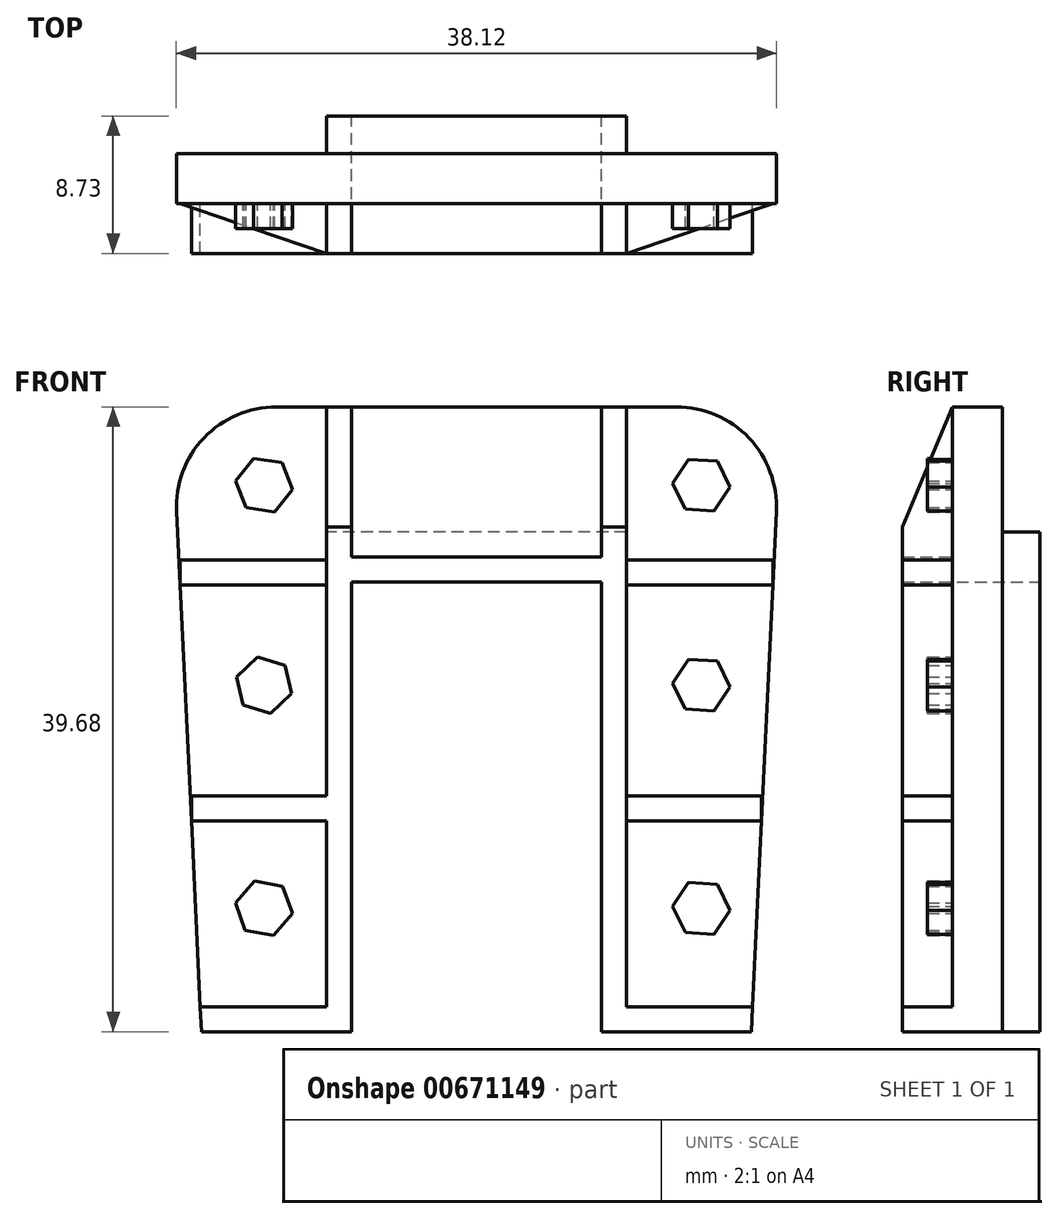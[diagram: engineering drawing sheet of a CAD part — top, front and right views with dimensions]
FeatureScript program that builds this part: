
annotation { "Feature Type Name" : "Feature", "Feature Type Description" : "" }
export const myFeature = defineFeature(function(context is Context, id is Id, definition is map)
    precondition{}
    {
        {
            var Q0;
            Q0=qCreatedBy(makeId("Front.planeOp"),FACE);
            var sketch = newSketch(context, id + "F0", { "sketchPlane" : qUnion([Q0])});
            skLineSegment(sketch, "E0", {"start": v(18.33, 6.17) * mm, "end": v(18.33, 34.74) * mm});
            skLineSegment(sketch, "E1", {"start": v(18.33, 34.74) * mm, "end": v(34.2, 34.74) * mm});
            skLineSegment(sketch, "E2", {"start": v(34.2, 34.74) * mm, "end": v(34.2, 6.17) * mm});
            skLineSegment(sketch, "E3", {"start": v(34.2, 6.17) * mm, "end": v(43.73, 6.17) * mm});
            skLineSegment(sketch, "E4", {"start": v(43.73, 6.17) * mm, "end": v(45.32, 39.2) * mm});
            skLineSegment(sketch, "E5", {"start": v(38.98, 45.85) * mm, "end": v(13.56, 45.85) * mm});
            skLineSegment(sketch, "E6", {"start": v(7.22, 39.2) * mm, "end": v(8.8, 6.17) * mm});
            skLineSegment(sketch, "E7", {"start": v(8.8, 6.17) * mm, "end": v(18.33, 6.17) * mm});
            skPoint(sketch, "E8.visualSharp", {"position": v(6.9, 45.85) * mm});
            skArc(sketch, "E8.filletArc", {"start": v(13.56, 45.85) * mm, "mid": v(8.97, 43.88) * mm, "end": v(7.22, 39.2) * mm});
            skPoint(sketch, "E9.visualSharp", {"position": v(45.64, 45.85) * mm});
            skArc(sketch, "E9.filletArc", {"start": v(45.32, 39.2) * mm, "mid": v(43.57, 43.88) * mm, "end": v(38.98, 45.85) * mm});
            skSolve(sketch);
        }
        {
            var Q0;
            Q0=qSketchRegion(id+"F0",true);
            extrude(context, id + "F1", {"entities" : qUnion([Q0]), "depth" : 3.17 * mm});
        }
        {
            var Q0;
            Q0=makeQuery(id+"F1.opExtrude","CAP_FACE",FACE,{"disambiguationData":[OSD([sQuery(id+"F0.wireOp",EDGE,"E0"),sQuery(id+"F0.wireOp",EDGE,"E1"),sQuery(id+"F0.wireOp",EDGE,"E2"),sQuery(id+"F0.wireOp",EDGE,"E3"),sQuery(id+"F0.wireOp",EDGE,"E4"),sQuery(id+"F0.wireOp",EDGE,"E5"),sQuery(id+"F0.wireOp",EDGE,"E6"),sQuery(id+"F0.wireOp",EDGE,"E7"),sQuery(id+"F0.wireOp",EDGE,"E8.filletArc"),sQuery(id+"F0.wireOp",EDGE,"E9.filletArc")])],"isStart":true});
            var sketch = newSketch(context, id + "F2", { "sketchPlane" : qUnion([Q0])});
            skLineSegment(sketch, "E10", {"start": v(-35.8, 6.17) * mm, "end": v(-35.8, 37.92) * mm});
            skLineSegment(sketch, "E11", {"start": v(-35.8, 37.92) * mm, "end": v(-16.75, 37.92) * mm});
            skLineSegment(sketch, "E12", {"start": v(-16.75, 37.92) * mm, "end": v(-16.75, 6.17) * mm});
            skSolve(sketch);
        }
        {
            var Q0;
            {var subQ2=sQuery(id+"F2.wireOp",EDGE,"E10");Q0=makeQuery(id+"F2.imprint","IMPRINT",FACE,{"disambiguationData":[TD([[makeQuery(id+"F2.imprint","IMPRINT",EDGE,{"derivedFrom":subQ2}),-1.0]])]});}
            extrude(context, id + "F3", {"entities" : qUnion([Q0]), "operationType" : NewBodyOperationType.ADD, "depth" : 2.38 * mm});
        }
        {
            var Q0;
            Q0=makeQuery(id+"F1.opExtrude","CAP_FACE",FACE,{"disambiguationData":[OSD([sQuery(id+"F0.wireOp",EDGE,"E0"),sQuery(id+"F0.wireOp",EDGE,"E1"),sQuery(id+"F0.wireOp",EDGE,"E2"),sQuery(id+"F0.wireOp",EDGE,"E3"),sQuery(id+"F0.wireOp",EDGE,"E4"),sQuery(id+"F0.wireOp",EDGE,"E5"),sQuery(id+"F0.wireOp",EDGE,"E6"),sQuery(id+"F0.wireOp",EDGE,"E7"),sQuery(id+"F0.wireOp",EDGE,"E8.filletArc"),sQuery(id+"F0.wireOp",EDGE,"E9.filletArc")])],"isStart":false});
            var sketch = newSketch(context, id + "F4", { "sketchPlane" : qUnion([Q0])});
            skLineSegment(sketch, "E13", {"start": v(8.73, 7.75) * mm, "end": v(16.75, 7.75) * mm});
            skLineSegment(sketch, "E14", {"start": v(16.75, 7.75) * mm, "end": v(16.75, 36.33) * mm});
            skLineSegment(sketch, "E15", {"start": v(16.75, 36.33) * mm, "end": v(35.8, 36.33) * mm});
            skLineSegment(sketch, "E16", {"start": v(35.8, 36.33) * mm, "end": v(35.8, 7.75) * mm});
            skLineSegment(sketch, "E17", {"start": v(35.8, 7.75) * mm, "end": v(43.8, 7.75) * mm});
            skSolve(sketch);
        }
        {
            var Q0;
            Q0=qSketchRegion(id+"F4",true);
            var Q1;
            {var subQ2=sQuery(id+"F4.wireOp",EDGE,"E13");Q1=makeQuery(id+"F4.imprint","IMPRINT",FACE,{"disambiguationData":[TD([[makeQuery(id+"F4.imprint","IMPRINT",EDGE,{"derivedFrom":subQ2}),-1.0]])]});}
            extrude(context, id + "F5", {"entities" : qUnion([Q0, Q1]), "operationType" : NewBodyOperationType.ADD, "depth" : 3.17 * mm});
        }
        {
            var Q0;
            Q0=makeQuery(id+"F1.opExtrude","CAP_FACE",FACE,{"disambiguationData":[OSD([sQuery(id+"F0.wireOp",EDGE,"E0"),sQuery(id+"F0.wireOp",EDGE,"E1"),sQuery(id+"F0.wireOp",EDGE,"E2"),sQuery(id+"F0.wireOp",EDGE,"E3"),sQuery(id+"F0.wireOp",EDGE,"E4"),sQuery(id+"F0.wireOp",EDGE,"E5"),sQuery(id+"F0.wireOp",EDGE,"E6"),sQuery(id+"F0.wireOp",EDGE,"E7"),sQuery(id+"F0.wireOp",EDGE,"E8.filletArc"),sQuery(id+"F0.wireOp",EDGE,"E9.filletArc")])],"isStart":false});
            var sketch = newSketch(context, id + "F6", { "sketchPlane" : qUnion([Q0])});
            skLineSegment(sketch, "E18", {"start": v(16.75, 36.33) * mm, "end": v(16.75, 45.85) * mm});
            skLineSegment(sketch, "E19", {"start": v(18.33, 36.33) * mm, "end": v(18.33, 45.85) * mm});
            skLineSegment(sketch, "E20", {"start": v(16.75, 36.12) * mm, "end": v(7.37, 36.12) * mm});
            skLineSegment(sketch, "E21", {"start": v(16.75, 34.53) * mm, "end": v(7.45, 34.53) * mm});
            skLineSegment(sketch, "E22", {"start": v(16.75, 21.15) * mm, "end": v(8.09, 21.15) * mm});
            skLineSegment(sketch, "E23", {"start": v(16.75, 19.56) * mm, "end": v(8.16, 19.56) * mm});
            skLineSegment(sketch, "E24", {"start": v(7.45, 34.53) * mm, "end": v(7.45, 36.12) * mm});
            skLineSegment(sketch, "E25", {"start": v(8.16, 19.56) * mm, "end": v(8.16, 21.15) * mm});
            skLineSegment(sketch, "E26", {"start": v(26.27, 36.24) * mm, "end": v(26.27, 28.66) * mm});
            skPoint(sketch, "E26.startSnap0", {"position": v(26.27, 36.33) * mm});
            skLineSegment(sketch, "E27.MirrorCS", {"start": v(34.2, 36.33) * mm, "end": v(34.2, 45.85) * mm});
            skLineSegment(sketch, "E28.MirrorCS", {"start": v(35.8, 36.33) * mm, "end": v(35.8, 45.85) * mm});
            skLineSegment(sketch, "E29.MirrorCS", {"start": v(35.8, 36.12) * mm, "end": v(45.17, 36.12) * mm});
            skLineSegment(sketch, "E30.MirrorCS", {"start": v(35.8, 34.53) * mm, "end": v(45.1, 34.53) * mm});
            skLineSegment(sketch, "E31.MirrorCS", {"start": v(45.1, 34.53) * mm, "end": v(45.1, 36.12) * mm});
            skLineSegment(sketch, "E32.MirrorCS", {"start": v(35.8, 21.15) * mm, "end": v(44.45, 21.15) * mm});
            skLineSegment(sketch, "E33.MirrorCS", {"start": v(44.38, 19.56) * mm, "end": v(44.38, 21.15) * mm});
            skLineSegment(sketch, "E34.MirrorCS", {"start": v(35.8, 19.56) * mm, "end": v(44.38, 19.56) * mm});
            skSolve(sketch);
        }
        {
            var Q0;
            Q0=qSketchRegion(id+"F6",true);
            var Q1;
            {var subQ4=sQuery(id+"F6.wireOp",EDGE,"E23");Q1=makeQuery(id+"F6.imprint","IMPRINT",FACE,{"disambiguationData":[TD([[makeQuery(id+"F6.imprint","IMPRINT",EDGE,{"derivedFrom":subQ4}),-1.0]])]});}
            var Q2;
            {var subQ4=sQuery(id+"F6.wireOp",EDGE,"E21");Q2=makeQuery(id+"F6.imprint","IMPRINT",FACE,{"disambiguationData":[TD([[makeQuery(id+"F6.imprint","IMPRINT",EDGE,{"derivedFrom":subQ4}),-1.0]])]});}
            var Q3;
            {var subQ0=sQuery(id+"F6.wireOp",EDGE,"E18");Q3=makeQuery(id+"F6.imprint","IMPRINT",FACE,{"disambiguationData":[TD([[makeQuery(id+"F6.imprint","IMPRINT",EDGE,{"derivedFrom":subQ0}),-1.0]])]});}
            var Q4;
            {var subQ0=sQuery(id+"F6.wireOp",EDGE,"E27.MirrorCS");Q4=makeQuery(id+"F6.imprint","IMPRINT",FACE,{"disambiguationData":[TD([[makeQuery(id+"F6.imprint","IMPRINT",EDGE,{"derivedFrom":subQ0}),-1.0]])]});}
            var Q5;
            {var subQ4=sQuery(id+"F6.wireOp",EDGE,"E30.MirrorCS");Q5=makeQuery(id+"F6.imprint","IMPRINT",FACE,{"disambiguationData":[TD([[makeQuery(id+"F6.imprint","IMPRINT",EDGE,{"derivedFrom":subQ4}),1.0]])]});}
            var Q6;
            {var subQ3=sQuery(id+"F6.wireOp",EDGE,"E33.MirrorCS");Q6=makeQuery(id+"F6.imprint","IMPRINT",FACE,{"disambiguationData":[TD([[makeQuery(id+"F6.imprint","IMPRINT",EDGE,{"derivedFrom":subQ3}),1.0]])]});}
            extrude(context, id + "F7", {"entities" : qUnion([Q0, Q1, Q2, Q3, Q4, Q5, Q6]), "operationType" : NewBodyOperationType.ADD, "depth" : 3.17 * mm});
        }
        {
            var Q0;
            Q0=makeQuery(id+"F7.boolean.opBoolean","MERGE",FACE,{"disambiguationData":[OD(1.0)],"derivedFrom":[makeQuery(id+"F5.opExtrude","SWEPT_FACE",FACE,{"disambiguationData":[OSD([sQuery(id+"F4.wireOp",EDGE,"E16")])]}),makeQuery(id+"F7.opExtrude","SWEPT_FACE",FACE,{"disambiguationData":[OSD([sQuery(id+"F6.wireOp",EDGE,"E28.MirrorCS")])]})]});
            var sketch = newSketch(context, id + "F8", { "sketchPlane" : qUnion([Q0])});
            skLineSegment(sketch, "E35", {"start": v(-3.17, 45.85) * mm, "end": v(-6.35, 38.23) * mm});
            skSolve(sketch);
        }
        {
            var Q0;
            Q0=qSketchRegion(id+"F8",true);
            var Q1;
            {var subQ0=sQuery(id+"F8.wireOp",EDGE,"E35");Q1=makeQuery(id+"F8.imprint","IMPRINT",FACE,{"disambiguationData":[TD([[makeQuery(id+"F8.imprint","IMPRINT",EDGE,{"derivedFrom":subQ0}),-1.0]])]});}
            extrude(context, id + "F9", {"entities" : qUnion([Q0, Q1]), "operationType" : NewBodyOperationType.REMOVE, "oppositeDirection" : true, "depth" : 25.4 * mm});
        }
        {
            var Q0;
            Q0=makeQuery(id+"F7.opExtrude","SWEPT_FACE",FACE,{"disambiguationData":[OSD([sQuery(id+"F6.wireOp",EDGE,"E29.MirrorCS")])]});
            var sketch = newSketch(context, id + "F10", { "sketchPlane" : qUnion([Q0])});
            skLineSegment(sketch, "E36", {"start": v(35.8, -6.35) * mm, "end": v(45.1, -3.18) * mm});
            skSolve(sketch);
        }
        {
            var Q0;
            Q0=qSketchRegion(id+"F10",true);
            var Q1;
            Q1=makeQuery(id+"F10.imprint","IMPRINT",FACE,{"disambiguationData":[TD([[makeQuery(id+"F10.imprint","IMPRINT",EDGE,{"derivedFrom":sQuery(id+"F10.wireOp",EDGE,"E36")}),-1.0]])]});
            extrude(context, id + "F11", {"entities" : qUnion([Q0, Q1]), "operationType" : NewBodyOperationType.REMOVE, "oppositeDirection" : true, "depth" : 3.17 * mm});
        }
        {
            var Q0;
            Q0=makeQuery(id+"F7.opExtrude","SWEPT_FACE",FACE,{"disambiguationData":[OSD([sQuery(id+"F6.wireOp",EDGE,"E32.MirrorCS")])]});
            var sketch = newSketch(context, id + "F12", { "sketchPlane" : qUnion([Q0])});
            skLineSegment(sketch, "E37", {"start": v(35.8, -6.35) * mm, "end": v(44.38, -3.18) * mm});
            skSolve(sketch);
        }
        {
            var Q0;
            Q0=qSketchRegion(id+"F12",true);
            var Q1;
            Q1=makeQuery(id+"F12.imprint","IMPRINT",FACE,{"disambiguationData":[TD([[makeQuery(id+"F12.imprint","IMPRINT",EDGE,{"derivedFrom":sQuery(id+"F12.wireOp",EDGE,"E37")}),-1.0]])]});
            extrude(context, id + "F13", {"entities" : qUnion([Q0, Q1]), "operationType" : NewBodyOperationType.REMOVE, "oppositeDirection" : true, "depth" : 1.59 * mm});
        }
        {
            var Q0;
            Q0=makeQuery(id+"F7.opExtrude","SWEPT_FACE",FACE,{"disambiguationData":[OSD([sQuery(id+"F6.wireOp",EDGE,"E20")])]});
            var sketch = newSketch(context, id + "F14", { "sketchPlane" : qUnion([Q0])});
            skLineSegment(sketch, "E38", {"start": v(7.45, -3.17) * mm, "end": v(16.75, -6.35) * mm});
            skSolve(sketch);
        }
        {
            var Q0;
            Q0=qSketchRegion(id+"F14",true);
            var Q1;
            Q1=makeQuery(id+"F14.imprint","IMPRINT",FACE,{"disambiguationData":[TD([[makeQuery(id+"F14.imprint","IMPRINT",EDGE,{"derivedFrom":sQuery(id+"F14.wireOp",EDGE,"E38")}),-1.0]])]});
            extrude(context, id + "F15", {"entities" : qUnion([Q0, Q1]), "operationType" : NewBodyOperationType.REMOVE, "oppositeDirection" : true, "depth" : 1.59 * mm});
        }
        {
            var Q0;
            {var subQ0=sQuery(id+"F0.wireOp",EDGE,"E6");var subQ2=sQuery(id+"F0.wireOp",EDGE,"E8.filletArc");var subQ3=sQuery(id+"F0.wireOp",EDGE,"E5");var subQ4=makeQuery(id+"F1.opExtrude","CAP_FACE",FACE,{"disambiguationData":[OSD([sQuery(id+"F0.wireOp",EDGE,"E0"),sQuery(id+"F0.wireOp",EDGE,"E1"),sQuery(id+"F0.wireOp",EDGE,"E2"),sQuery(id+"F0.wireOp",EDGE,"E3"),sQuery(id+"F0.wireOp",EDGE,"E4"),subQ3,subQ0,sQuery(id+"F0.wireOp",EDGE,"E7"),subQ2,sQuery(id+"F0.wireOp",EDGE,"E9.filletArc")])],"isStart":false});Q0=makeQuery(id+"F7.boolean.opBoolean","SPLIT",FACE,{"disambiguationData":[TD([makeQuery(id+"F1.opExtrude","SWEPT_FACE",FACE,{"disambiguationData":[OSD([subQ2])]})])],"derivedFrom":subQ4});}
            var sketch = newSketch(context, id + "F16", { "sketchPlane" : qUnion([Q0])});
            skCircle(sketch, "E39.cCircle", {"center": v(12.78, 40.88) * mm, "radius": 1.59 * mm, "construction": true});
            skLineSegment(sketch, "E39.0", {"start": v(14.59, 40.6) * mm, "end": v(13.44, 39.17) * mm});
            skLineSegment(sketch, "E39.1", {"start": v(13.44, 39.17) * mm, "end": v(11.63, 39.45) * mm});
            skLineSegment(sketch, "E39.2", {"start": v(11.63, 39.45) * mm, "end": v(10.97, 41.16) * mm});
            skLineSegment(sketch, "E39.3", {"start": v(10.97, 41.16) * mm, "end": v(12.12, 42.59) * mm});
            skLineSegment(sketch, "E39.4", {"start": v(12.12, 42.59) * mm, "end": v(13.93, 42.3) * mm});
            skLineSegment(sketch, "E39.5", {"start": v(13.93, 42.3) * mm, "end": v(14.59, 40.6) * mm});
            skPoint(sketch, "E39.0.midPoint", {"position": v(14.01, 39.88) * mm});
            skCircle(sketch, "E40.cCircle", {"center": v(40.56, 40.88) * mm, "radius": 1.59 * mm, "construction": true});
            skLineSegment(sketch, "E40.0", {"start": v(42.39, 40.76) * mm, "end": v(41.37, 39.23) * mm});
            skLineSegment(sketch, "E40.1", {"start": v(41.37, 39.23) * mm, "end": v(39.54, 39.35) * mm});
            skLineSegment(sketch, "E40.2", {"start": v(39.54, 39.35) * mm, "end": v(38.73, 41) * mm});
            skLineSegment(sketch, "E40.3", {"start": v(38.73, 41) * mm, "end": v(39.75, 42.52) * mm});
            skLineSegment(sketch, "E40.4", {"start": v(39.75, 42.52) * mm, "end": v(41.58, 42.4) * mm});
            skLineSegment(sketch, "E40.5", {"start": v(41.58, 42.4) * mm, "end": v(42.39, 40.76) * mm});
            skPoint(sketch, "E40.0.midPoint", {"position": v(41.88, 40) * mm});
            skCircle(sketch, "E41.cCircle", {"center": v(12.78, 28.18) * mm, "radius": 1.59 * mm, "construction": true});
            skLineSegment(sketch, "E41.0", {"start": v(14.53, 27.65) * mm, "end": v(13.2, 26.4) * mm});
            skLineSegment(sketch, "E41.1", {"start": v(13.2, 26.4) * mm, "end": v(11.44, 26.92) * mm});
            skLineSegment(sketch, "E41.2", {"start": v(11.44, 26.92) * mm, "end": v(11.02, 28.7) * mm});
            skLineSegment(sketch, "E41.3", {"start": v(11.02, 28.7) * mm, "end": v(12.36, 29.96) * mm});
            skLineSegment(sketch, "E41.4", {"start": v(12.36, 29.96) * mm, "end": v(14.11, 29.43) * mm});
            skLineSegment(sketch, "E41.5", {"start": v(14.11, 29.43) * mm, "end": v(14.53, 27.65) * mm});
            skPoint(sketch, "E41.0.midPoint", {"position": v(13.86, 27.02) * mm});
            skCircle(sketch, "E42.cCircle", {"center": v(40.56, 28.18) * mm, "radius": 1.59 * mm, "construction": true});
            skLineSegment(sketch, "E42.0", {"start": v(42.39, 28.06) * mm, "end": v(41.37, 26.53) * mm});
            skLineSegment(sketch, "E42.1", {"start": v(41.37, 26.53) * mm, "end": v(39.54, 26.65) * mm});
            skLineSegment(sketch, "E42.2", {"start": v(39.54, 26.65) * mm, "end": v(38.73, 28.3) * mm});
            skLineSegment(sketch, "E42.3", {"start": v(38.73, 28.3) * mm, "end": v(39.75, 29.82) * mm});
            skLineSegment(sketch, "E42.4", {"start": v(39.75, 29.82) * mm, "end": v(41.58, 29.7) * mm});
            skLineSegment(sketch, "E42.5", {"start": v(41.58, 29.7) * mm, "end": v(42.39, 28.06) * mm});
            skPoint(sketch, "E42.0.midPoint", {"position": v(41.88, 27.3) * mm});
            skCircle(sketch, "E43.cCircle", {"center": v(12.78, 14) * mm, "radius": 1.59 * mm, "construction": true});
            skLineSegment(sketch, "E43.0", {"start": v(14.58, 13.67) * mm, "end": v(13.39, 12.28) * mm});
            skLineSegment(sketch, "E43.1", {"start": v(13.39, 12.28) * mm, "end": v(11.59, 12.61) * mm});
            skLineSegment(sketch, "E43.2", {"start": v(11.59, 12.61) * mm, "end": v(10.97, 14.34) * mm});
            skLineSegment(sketch, "E43.3", {"start": v(10.97, 14.34) * mm, "end": v(12.16, 15.74) * mm});
            skLineSegment(sketch, "E43.4", {"start": v(12.16, 15.74) * mm, "end": v(13.97, 15.4) * mm});
            skLineSegment(sketch, "E43.5", {"start": v(13.97, 15.4) * mm, "end": v(14.58, 13.67) * mm});
            skPoint(sketch, "E43.0.midPoint", {"position": v(13.98, 12.98) * mm});
            skCircle(sketch, "E44.cCircle", {"center": v(40.56, 14) * mm, "radius": 1.59 * mm, "construction": true});
            skLineSegment(sketch, "E44.0", {"start": v(42.39, 13.89) * mm, "end": v(41.37, 12.36) * mm});
            skLineSegment(sketch, "E44.1", {"start": v(41.37, 12.36) * mm, "end": v(39.54, 12.48) * mm});
            skLineSegment(sketch, "E44.2", {"start": v(39.54, 12.48) * mm, "end": v(38.73, 14.13) * mm});
            skLineSegment(sketch, "E44.3", {"start": v(38.73, 14.13) * mm, "end": v(39.75, 15.65) * mm});
            skLineSegment(sketch, "E44.4", {"start": v(39.75, 15.65) * mm, "end": v(41.58, 15.53) * mm});
            skLineSegment(sketch, "E44.5", {"start": v(41.58, 15.53) * mm, "end": v(42.39, 13.89) * mm});
            skPoint(sketch, "E44.0.midPoint", {"position": v(41.88, 13.13) * mm});
            skSolve(sketch);
        }
        {
            var Q0;
            Q0=qSketchRegion(id+"F16",true);
            extrude(context, id + "F17", {"entities" : qUnion([Q0]), "operationType" : NewBodyOperationType.ADD, "depth" : 1.59 * mm});
        }
    });
